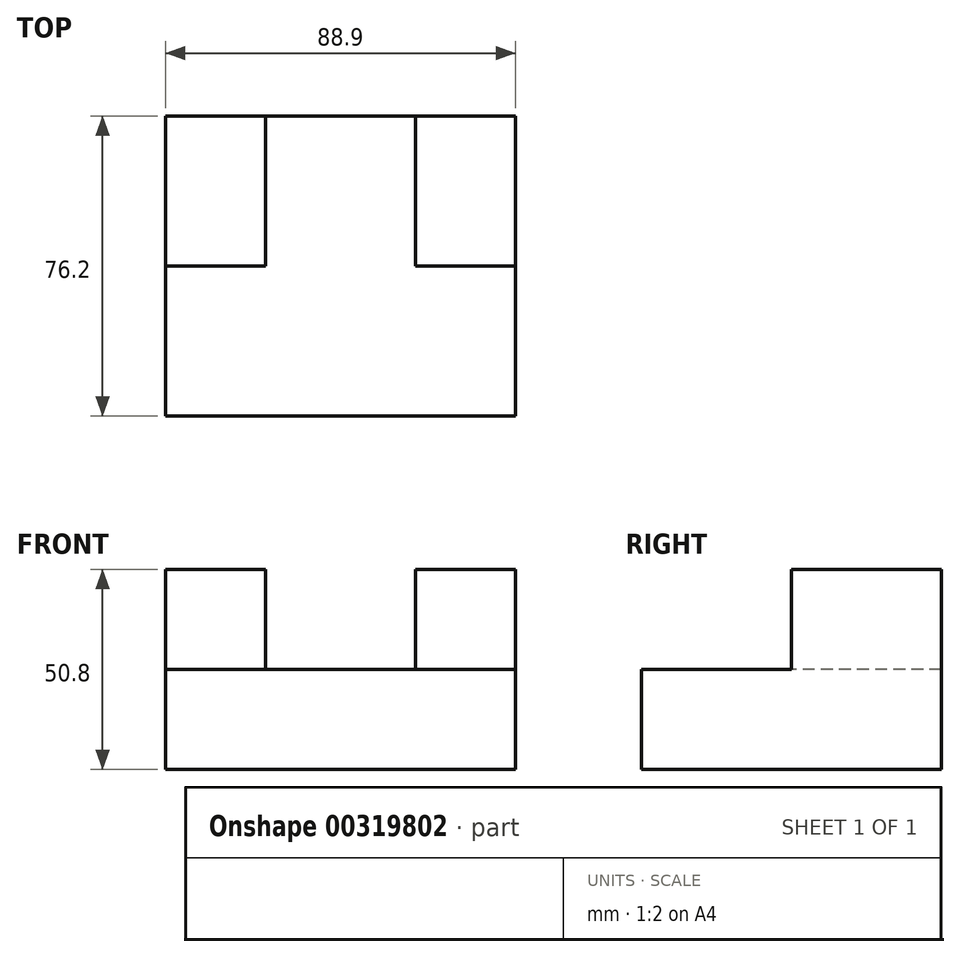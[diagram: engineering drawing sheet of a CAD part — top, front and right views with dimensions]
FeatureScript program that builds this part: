
annotation { "Feature Type Name" : "Feature", "Feature Type Description" : "" }
export const myFeature = defineFeature(function(context is Context, id is Id, definition is map)
    precondition{}
    {
        {
            var Q0;
            Q0=qCreatedBy(makeId("Top.planeOp"),FACE);
            var sketch = newSketch(context, id + "F0", { "sketchPlane" : qUnion([Q0])});
            skLineSegment(sketch, "E0", {"start": v(-45.36, -16.6) * mm, "end": v(43.54, -16.6) * mm});
            skLineSegment(sketch, "E1", {"start": v(43.54, -16.6) * mm, "end": v(43.54, 59.6) * mm});
            skLineSegment(sketch, "E2", {"start": v(43.54, 59.6) * mm, "end": v(-45.36, 59.6) * mm});
            skLineSegment(sketch, "E3", {"start": v(-45.36, 59.6) * mm, "end": v(-45.36, -16.6) * mm});
            skSolve(sketch);
        }
        {
            var Q0;
            Q0=makeQuery(id+"F0.imprint","IMPRINT",FACE,{"disambiguationData":[TD([[makeQuery(id+"F0.imprint","IMPRINT",EDGE,{"derivedFrom":sQuery(id+"F0.wireOp",EDGE,"E0")}),1.0]])]});
            extrude(context, id + "F1", {"entities" : qUnion([Q0]), "depth" : 25.4 * mm});
        }
        {
            var Q0;
            Q0=makeQuery(id+"F1.opExtrude","CAP_FACE",FACE,{"disambiguationData":[OSD([sQuery(id+"F0.wireOp",EDGE,"E0"),sQuery(id+"F0.wireOp",EDGE,"E1"),sQuery(id+"F0.wireOp",EDGE,"E2"),sQuery(id+"F0.wireOp",EDGE,"E3")])],"isStart":false});
            var sketch = newSketch(context, id + "F2", { "sketchPlane" : qUnion([Q0])});
            skLineSegment(sketch, "E4.bottom", {"start": v(-45.36, 59.6) * mm, "end": v(-19.96, 59.6) * mm});
            skLineSegment(sketch, "E4.top", {"start": v(-45.36, 21.5) * mm, "end": v(-19.96, 21.5) * mm});
            skLineSegment(sketch, "E4.left", {"start": v(-45.36, 59.6) * mm, "end": v(-45.36, 21.5) * mm});
            skLineSegment(sketch, "E4.right", {"start": v(-19.96, 59.6) * mm, "end": v(-19.96, 21.5) * mm});
            skLineSegment(sketch, "E5.bottom", {"start": v(43.54, 59.6) * mm, "end": v(18.14, 59.6) * mm});
            skLineSegment(sketch, "E5.top", {"start": v(43.54, 21.5) * mm, "end": v(18.14, 21.5) * mm});
            skLineSegment(sketch, "E5.left", {"start": v(43.54, 59.6) * mm, "end": v(43.54, 21.5) * mm});
            skLineSegment(sketch, "E5.right", {"start": v(18.14, 59.6) * mm, "end": v(18.14, 21.5) * mm});
            skSolve(sketch);
        }
        {
            var Q0;
            Q0=makeQuery(id+"F2.imprint","IMPRINT",FACE,{"disambiguationData":[TD([[makeQuery(id+"F2.imprint","IMPRINT",EDGE,{"derivedFrom":sQuery(id+"F2.wireOp",EDGE,"E4.bottom")}),1.0]])]});
            var Q1;
            Q1=makeQuery(id+"F2.imprint","IMPRINT",FACE,{"disambiguationData":[TD([[makeQuery(id+"F2.imprint","IMPRINT",EDGE,{"derivedFrom":sQuery(id+"F2.wireOp",EDGE,"E5.bottom")}),1.0]])]});
            extrude(context, id + "F3", {"entities" : qUnion([Q0, Q1]), "operationType" : NewBodyOperationType.ADD, "depth" : 25.4 * mm});
        }
    });
